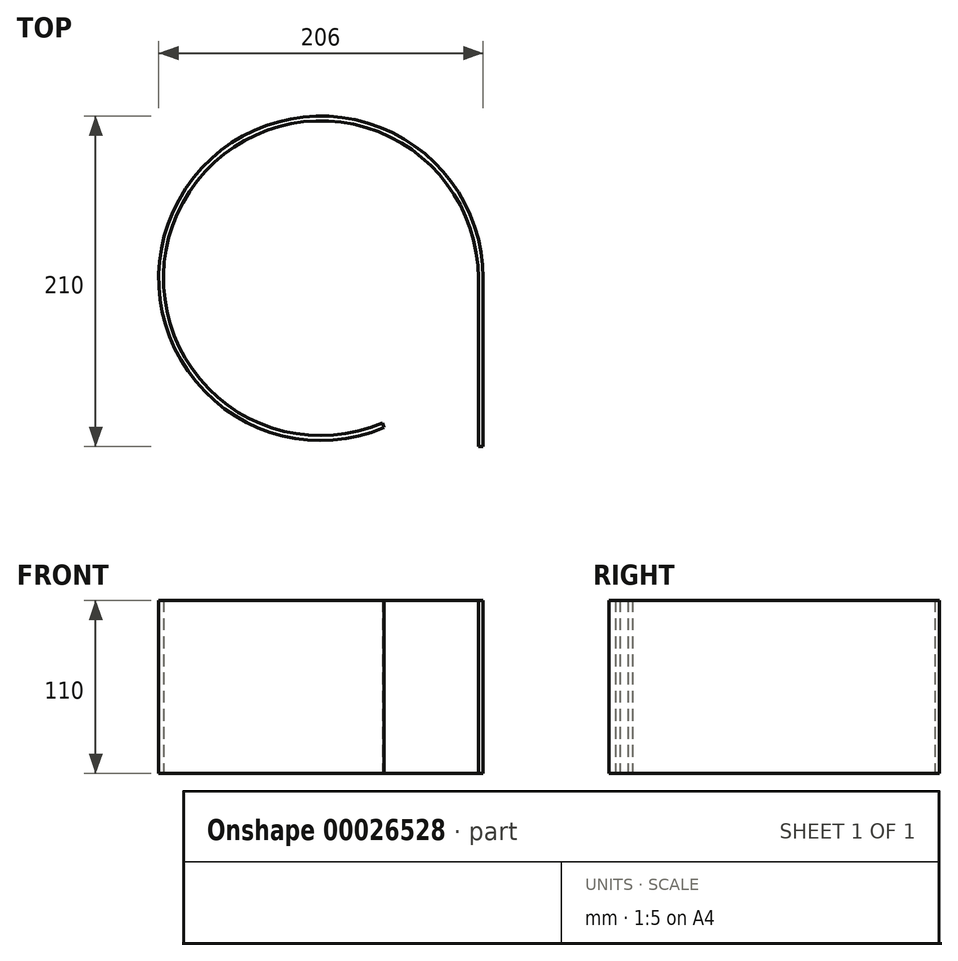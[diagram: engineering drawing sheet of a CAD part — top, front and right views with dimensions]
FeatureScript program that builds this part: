
annotation { "Feature Type Name" : "Feature", "Feature Type Description" : "" }
export const myFeature = defineFeature(function(context is Context, id is Id, definition is map)
    precondition{}
    {
        {
            var Q0;
            Q0=qCreatedBy(makeId("Top.planeOp"),FACE);
            var sketch = newSketch(context, id + "F0", { "sketchPlane" : qUnion([Q0])});
            skArc(sketch, "E0", {"start": v(5.4, 119.39) * mm, "mid": v(-133.76, 46.22) * mm, "end": v(-14.35, -56.06) * mm});
            skArc(sketch, "E1", {"start": v(60.64, 35.6) * mm, "mid": v(-122.78, 90.74) * mm, "end": v(-0.2, -56.42) * mm});
            skLineSegment(sketch, "E2", {"start": v(63.64, 35.6) * mm, "end": v(63.64, -89.4) * mm});
            skLineSegment(sketch, "E3", {"start": v(60.64, 35.6) * mm, "end": v(60.64, -71.4) * mm});
            skLineSegment(sketch, "E4", {"start": v(-17.36, -65.03) * mm, "end": v(-17.36, -89.4) * mm});
            skLineSegment(sketch, "E5", {"start": v(63.64, -71.4) * mm, "end": v(-17.36, -71.4) * mm});
            skLineSegment(sketch, "E6", {"start": v(85.64, 35.6) * mm, "end": v(85.53, -89.4) * mm});
            skLineSegment(sketch, "E7", {"start": v(-6.5, -39.68) * mm, "end": v(-6.91, -38.75) * mm});
            skLineSegment(sketch, "E8", {"start": v(8.8, 100.86) * mm, "end": v(9.4, 101.68) * mm});
            skArc(sketch, "E9", {"start": v(-6.5, 97.4) * mm, "mid": v(-108.92, 43.42) * mm, "end": v(-21.05, -31.97) * mm});
            skPoint(sketch, "E10.visualSharp", {"position": v(17.04, 112.03) * mm});
            skArc(sketch, "E10.filletArc", {"start": v(9.4, 101.68) * mm, "mid": v(11.45, 111.45) * mm, "end": v(5.4, 119.39) * mm});
            skPoint(sketch, "E11.visualSharp", {"position": v(2.2, 91.92) * mm});
            skArc(sketch, "E11.filletArc", {"start": v(-6.5, 97.4) * mm, "mid": v(1.8, 96.29) * mm, "end": v(8.8, 100.86) * mm});
            skPoint(sketch, "E12.visualSharp", {"position": v(-11.36, -28.57) * mm});
            skArc(sketch, "E12.filletArc", {"start": v(-6.91, -38.75) * mm, "mid": v(-12.72, -32.73) * mm, "end": v(-21.05, -31.97) * mm});
            skPoint(sketch, "E13.visualSharp", {"position": v(-1.36, -51.48) * mm});
            skArc(sketch, "E13.filletArc", {"start": v(-14.35, -56.06) * mm, "mid": v(-6.68, -49.66) * mm, "end": v(-6.5, -39.68) * mm});
            skLineSegment(sketch, "E14", {"start": v(0.64, -59.32) * mm, "end": v(-0.2, -56.42) * mm});
            skArc(sketch, "E15", {"start": v(85.64, 35.37) * mm, "mid": v(-127.67, 124.06) * mm, "end": v(-39.36, -89.4) * mm});
            skLineSegment(sketch, "E16", {"start": v(-39.36, -89.4) * mm, "end": v(-17.36, -89.4) * mm});
            skLineSegment(sketch, "E17", {"start": v(-17.36, -89.4) * mm, "end": v(85.53, -89.4) * mm});
            skLineSegment(sketch, "E18", {"start": v(60.64, -53.4) * mm, "end": v(12.49, -53.4) * mm});
            skArc(sketch, "E19", {"start": v(63.64, 35.6) * mm, "mid": v(-141.6, 48.02) * mm, "end": v(60.64, 10.91) * mm});
            skSolve(sketch);
        }
        {
            var Q0;
            {var subQ11=sQuery(id+"F0.wireOp",EDGE,"E1");Q0=makeQuery(id+"F0.imprint","IMPRINT",FACE,{"disambiguationData":[TD([[makeQuery(id+"F0.imprint","IMPRINT",EDGE,{"derivedFrom":subQ11}),-1.0]])]});}
            extrude(context, id + "F1", {"entities" : qUnion([Q0]), "depth" : 110 * mm});
        }
    });
